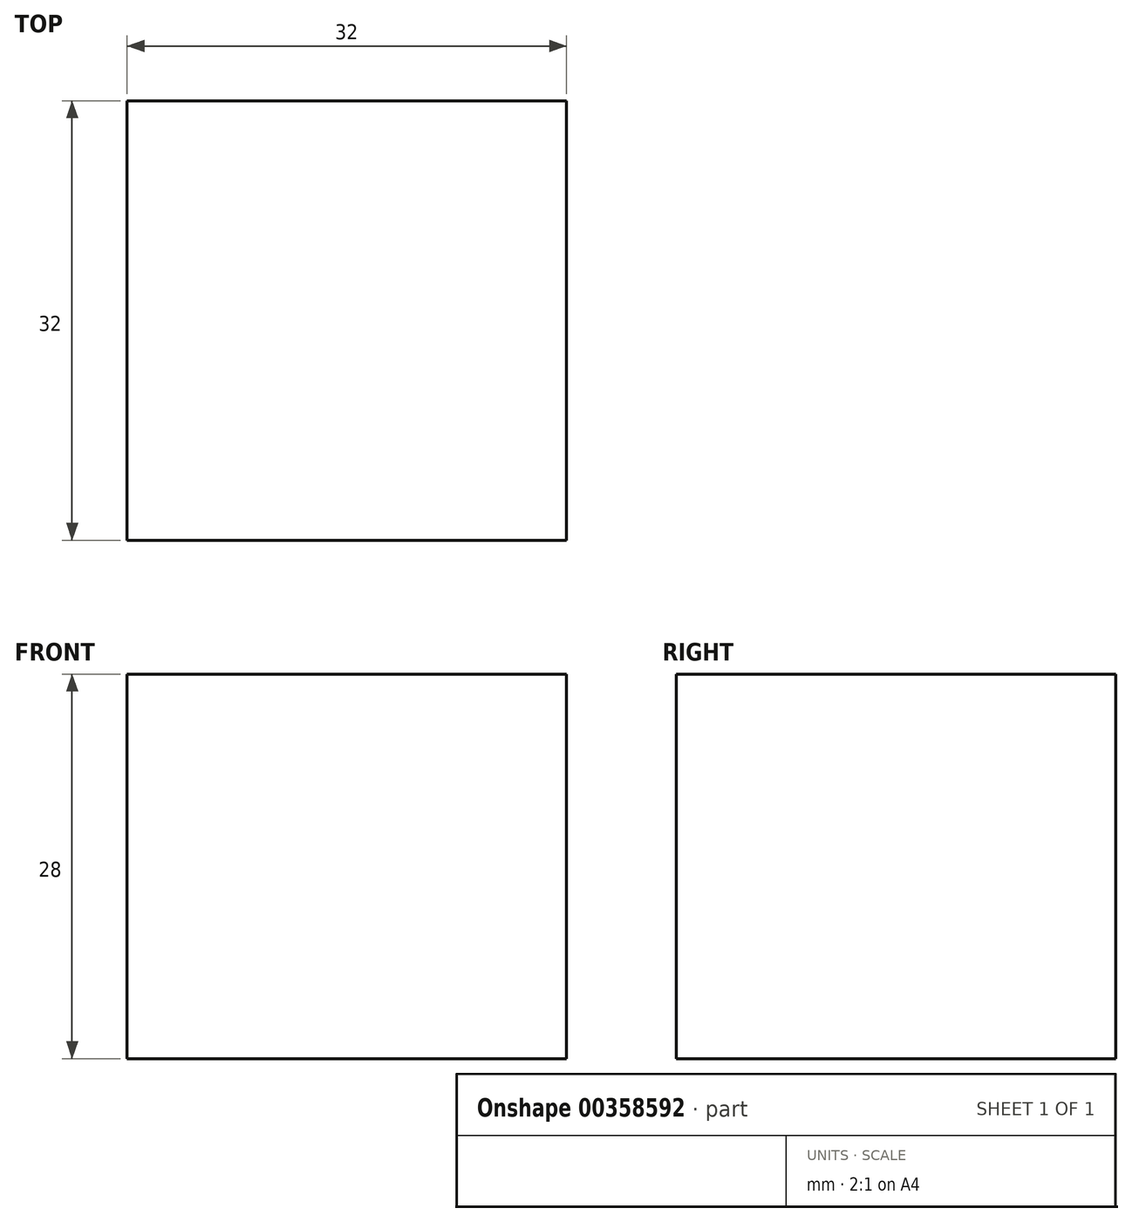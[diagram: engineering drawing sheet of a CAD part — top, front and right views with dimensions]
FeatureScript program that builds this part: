
annotation { "Feature Type Name" : "Feature", "Feature Type Description" : "" }
export const myFeature = defineFeature(function(context is Context, id is Id, definition is map)
    precondition{}
    {
        {
            var Q0;
            Q0=qCreatedBy(makeId("Front.planeOp"),FACE);
            var sketch = newSketch(context, id + "F0", { "sketchPlane" : qUnion([Q0])});
            skLineSegment(sketch, "E0.bottom", {"start": v(-16, 14) * mm, "end": v(16, 14) * mm});
            skLineSegment(sketch, "E0.top", {"start": v(-16, -14) * mm, "end": v(16, -14) * mm});
            skLineSegment(sketch, "E0.left", {"start": v(-16, 14) * mm, "end": v(-16, -14) * mm});
            skLineSegment(sketch, "E0.right", {"start": v(16, 14) * mm, "end": v(16, -14) * mm});
            skPoint(sketch, "E0.middle", {"position": v(0, 0) * mm});
            skSolve(sketch);
        }
        {
            var Q0;
            Q0 = qSketchRegion(id + "F0", true);
            extrude(context, id + "F1", {"entities" : qUnion([Q0]), "depth" : 32 * mm});
        }
    });
